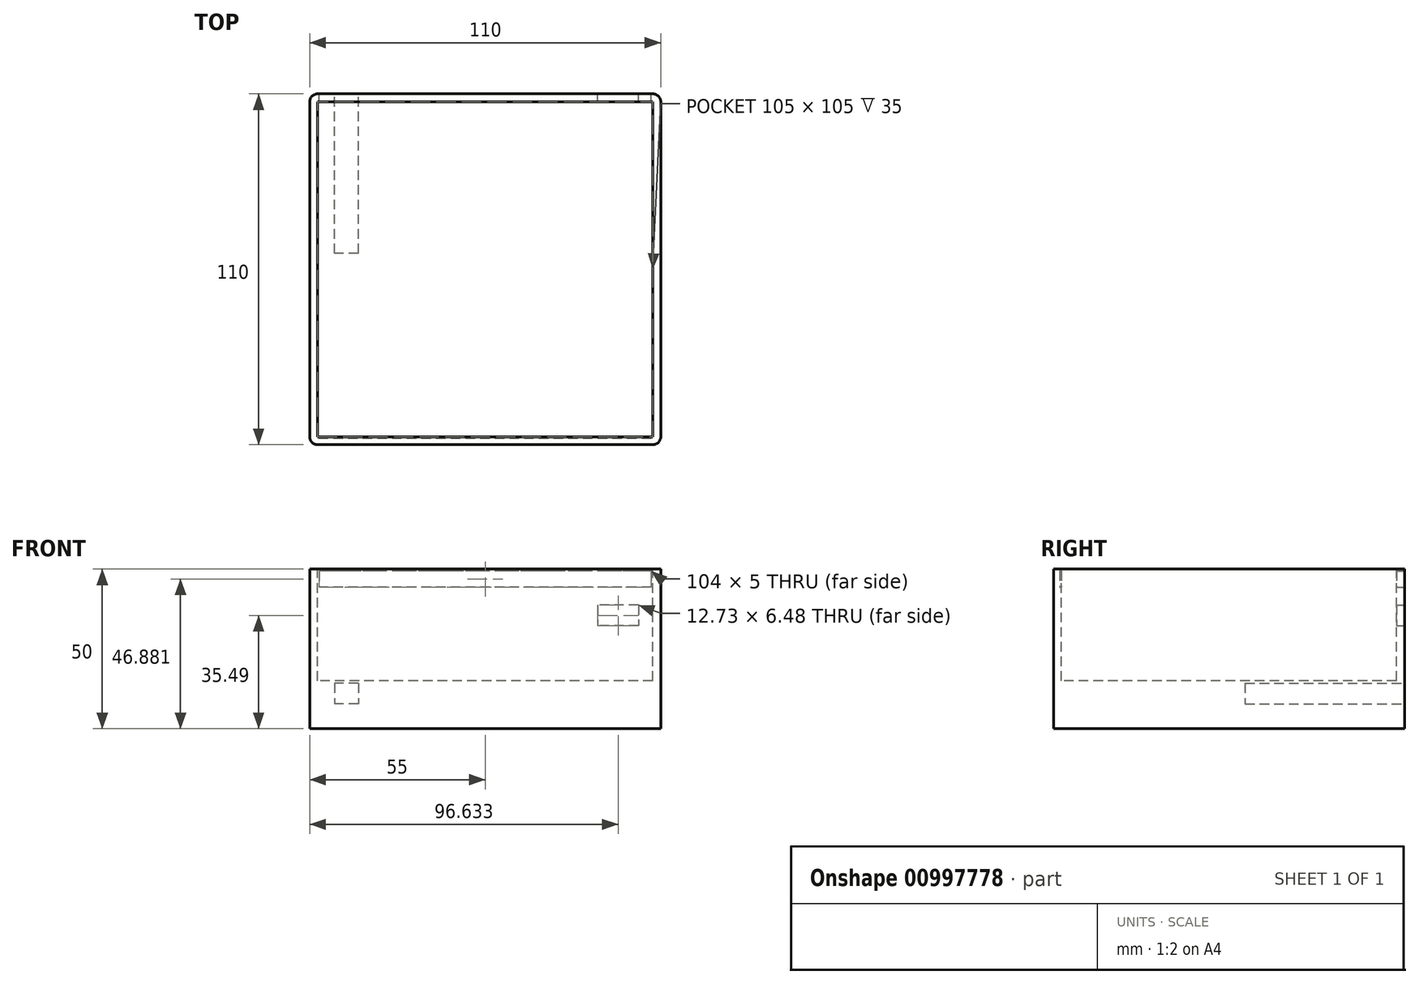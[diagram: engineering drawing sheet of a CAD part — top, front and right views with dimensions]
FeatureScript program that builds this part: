
annotation { "Feature Type Name" : "Feature", "Feature Type Description" : "" }
export const myFeature = defineFeature(function(context is Context, id is Id, definition is map)
    precondition{}
    {
        {
            var Q0;
            Q0=qCreatedBy(makeId("Top.planeOp"),FACE);
            var sketch = newSketch(context, id + "F0", { "sketchPlane" : qUnion([Q0])});
            skLineSegment(sketch, "E0.bottom", {"start": v(55, 55) * mm, "end": v(-55, 55) * mm});
            skLineSegment(sketch, "E0.top", {"start": v(55, -55) * mm, "end": v(-55, -55) * mm});
            skLineSegment(sketch, "E0.left", {"start": v(55, 55) * mm, "end": v(55, -55) * mm});
            skLineSegment(sketch, "E0.right", {"start": v(-55, 55) * mm, "end": v(-55, -55) * mm});
            skPoint(sketch, "E0.middle", {"position": v(0, 0) * mm});
            skSolve(sketch);
        }
        {
            var Q0;
            Q0=makeQuery(id+"F0.imprint","IMPRINT",FACE,{"disambiguationData":[TD([[makeQuery(id+"F0.imprint","IMPRINT",EDGE,{"derivedFrom":sQuery(id+"F0.wireOp",EDGE,"E0.bottom")}),1.0]])]});
            extrude(context, id + "F1", {"entities" : qUnion([Q0]), "depth" : 50 * mm, "offsetDistance" : 25 * mm});
        }
        {
            var Q0;
            Q0=makeQuery(id+"F1.opExtrude","CAP_FACE",FACE,{"disambiguationData":[OSD([sQuery(id+"F0.wireOp",EDGE,"E0.bottom"),sQuery(id+"F0.wireOp",EDGE,"E0.top"),sQuery(id+"F0.wireOp",EDGE,"E0.left"),sQuery(id+"F0.wireOp",EDGE,"E0.right")])],"isStart":false});
            var sketch = newSketch(context, id + "F2", { "sketchPlane" : qUnion([Q0])});
            skLineSegment(sketch, "E1.bottom", {"start": v(52.5, 52.5) * mm, "end": v(-52.5, 52.5) * mm});
            skLineSegment(sketch, "E1.top", {"start": v(52.5, -52.5) * mm, "end": v(-52.5, -52.5) * mm});
            skLineSegment(sketch, "E1.left", {"start": v(52.5, 52.5) * mm, "end": v(52.5, -52.5) * mm});
            skLineSegment(sketch, "E1.right", {"start": v(-52.5, 52.5) * mm, "end": v(-52.5, -52.5) * mm});
            skPoint(sketch, "E1.middle", {"position": v(0, 0) * mm});
            skSolve(sketch);
        }
        {
            var Q0;
            Q0 = qSketchRegion(id + "F2", true);
            extrude(context, id + "F3", {"entities" : qUnion([Q0]), "operationType" : NewBodyOperationType.REMOVE, "oppositeDirection" : true, "depth" : 35 * mm, "offsetDistance" : 25 * mm});
        }
        {
            var Q0;
            Q0=makeQuery(id+"F1.opExtrude","SWEPT_FACE",FACE,{"disambiguationData":[OSD([sQuery(id+"F0.wireOp",EDGE,"E0.bottom")])]});
            var sketch = newSketch(context, id + "F4", { "sketchPlane" : qUnion([Q0])});
            skLineSegment(sketch, "E2.bottom", {"start": v(-52, 49.38) * mm, "end": v(52, 49.38) * mm});
            skLineSegment(sketch, "E2.top", {"start": v(-52, 44.38) * mm, "end": v(52, 44.38) * mm});
            skLineSegment(sketch, "E2.left", {"start": v(-52, 49.38) * mm, "end": v(-52, 44.38) * mm});
            skLineSegment(sketch, "E2.right", {"start": v(52, 49.38) * mm, "end": v(52, 44.38) * mm});
            skSolve(sketch);
        }
        {
            var Q0;
            Q0 = qSketchRegion(id + "F4", true);
            extrude(context, id + "F5", {"entities" : qUnion([Q0]), "operationType" : NewBodyOperationType.REMOVE, "oppositeDirection" : true, "depth" : 108 * mm, "offsetDistance" : 25 * mm});
        }
        {
            var Q0;
            Q0=makeQuery(id+"F1.opExtrude","SWEPT_FACE",FACE,{"disambiguationData":[OSD([sQuery(id+"F0.wireOp",EDGE,"E0.bottom")])]});
            var sketch = newSketch(context, id + "F6", { "sketchPlane" : qUnion([Q0])});
            skLineSegment(sketch, "E3.bottom", {"start": v(-48, 38.73) * mm, "end": v(-35.27, 38.73) * mm});
            skLineSegment(sketch, "E3.top", {"start": v(-48, 32.25) * mm, "end": v(-35.27, 32.25) * mm});
            skLineSegment(sketch, "E3.left", {"start": v(-48, 38.73) * mm, "end": v(-48, 32.25) * mm});
            skLineSegment(sketch, "E3.right", {"start": v(-35.27, 38.73) * mm, "end": v(-35.27, 32.25) * mm});
            skLineSegment(sketch, "E4.bottom", {"start": v(39.76, 14.19) * mm, "end": v(47.16, 14.19) * mm});
            skLineSegment(sketch, "E4.top", {"start": v(39.76, 7.7) * mm, "end": v(47.16, 7.7) * mm});
            skLineSegment(sketch, "E4.left", {"start": v(39.76, 14.19) * mm, "end": v(39.76, 7.7) * mm});
            skLineSegment(sketch, "E4.right", {"start": v(47.16, 14.19) * mm, "end": v(47.16, 7.7) * mm});
            skSolve(sketch);
        }
        {
            var Q0;
            Q0 = qSketchRegion(id + "F6", true);
            extrude(context, id + "F7", {"entities" : qUnion([Q0]), "operationType" : NewBodyOperationType.REMOVE, "oppositeDirection" : true, "depth" : 50 * mm, "offsetDistance" : 25 * mm});
        }
        {
            var Q0;
            Q0=makeQuery(id+"F1.opExtrude","SWEPT_EDGE",EDGE,{"disambiguationData":[OSD([sQuery(id+"F0.wireOp",EDGE,"E0.bottom"),sQuery(id+"F0.wireOp",EDGE,"E0.right")])]});
            var Q1;
            Q1=makeQuery(id+"F1.opExtrude","SWEPT_EDGE",EDGE,{"disambiguationData":[OSD([sQuery(id+"F0.wireOp",EDGE,"E0.top"),sQuery(id+"F0.wireOp",EDGE,"E0.right")])]});
            var Q2;
            Q2=makeQuery(id+"F1.opExtrude","SWEPT_EDGE",EDGE,{"disambiguationData":[OSD([sQuery(id+"F0.wireOp",EDGE,"E0.bottom"),sQuery(id+"F0.wireOp",EDGE,"E0.left")])]});
            var Q3;
            Q3=makeQuery(id+"F1.opExtrude","SWEPT_EDGE",EDGE,{"disambiguationData":[OSD([sQuery(id+"F0.wireOp",EDGE,"E0.top"),sQuery(id+"F0.wireOp",EDGE,"E0.left")])]});
            fillet(context, id + "F8", {"entities" : qUnion([Q0, Q1, Q2, Q3]), "radius" : 2.5 * mm, "tangentPropagation" : true, "allowEdgeOverflow" : false});
        }
    });
